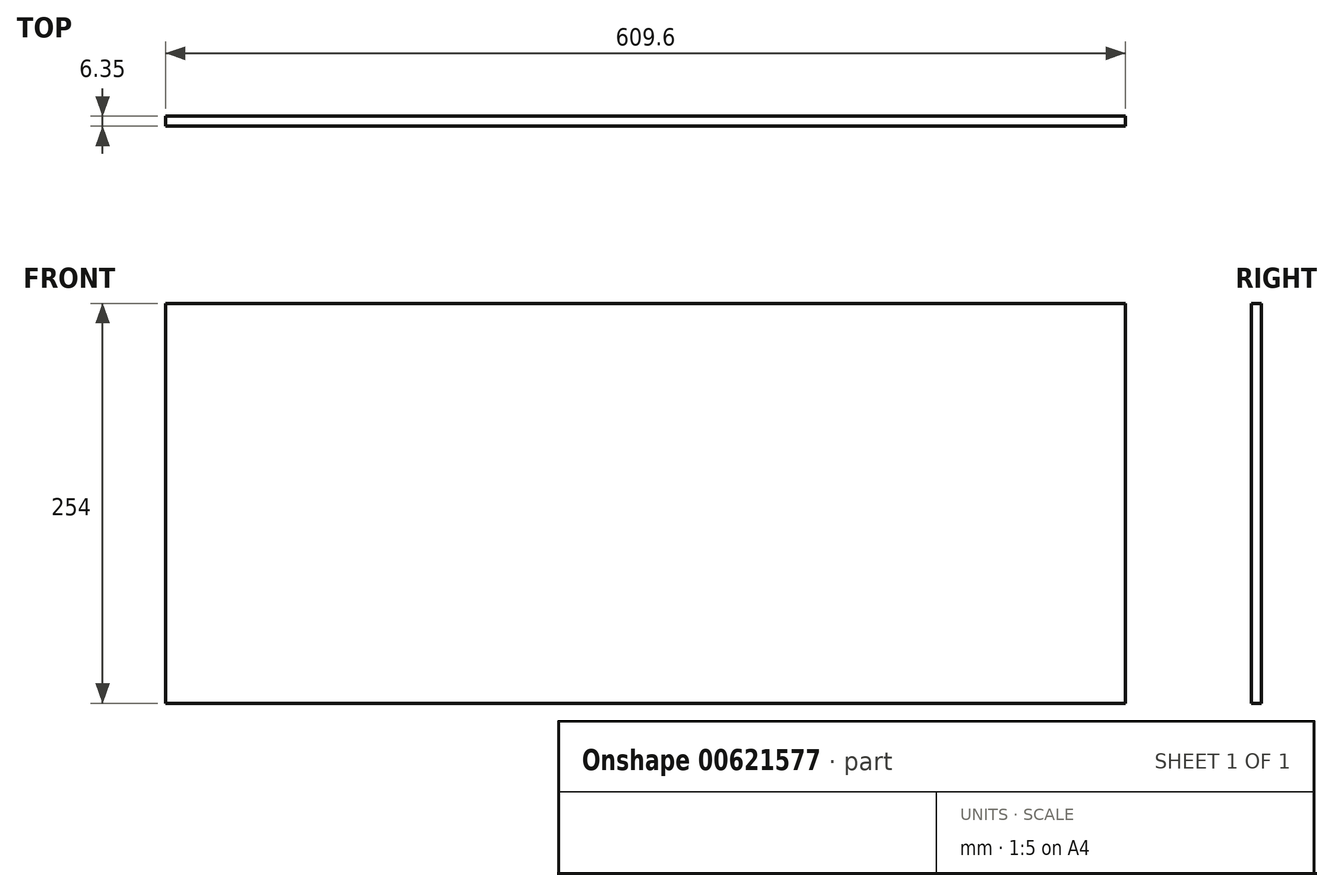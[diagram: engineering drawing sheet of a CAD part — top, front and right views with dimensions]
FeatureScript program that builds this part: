
annotation { "Feature Type Name" : "Feature", "Feature Type Description" : "" }
export const myFeature = defineFeature(function(context is Context, id is Id, definition is map)
    precondition{}
    {
        {
            var Q0;
            Q0=qCreatedBy(makeId("Front.planeOp"),FACE);
            var sketch = newSketch(context, id + "F0", { "sketchPlane" : qUnion([Q0])});
            skLineSegment(sketch, "E0.bottom", {"start": v(308.6, 127) * mm, "end": v(-301, 127) * mm});
            skLineSegment(sketch, "E0.top", {"start": v(308.6, -127) * mm, "end": v(-301, -127) * mm});
            skLineSegment(sketch, "E0.left", {"start": v(308.6, 127) * mm, "end": v(308.6, -127) * mm});
            skLineSegment(sketch, "E0.right", {"start": v(-301, 127) * mm, "end": v(-301, -127) * mm});
            skPoint(sketch, "E0.middle", {"position": v(3.8, 0) * mm});
            skSolve(sketch);
        }
        {
            var Q0;
            Q0 = qSketchRegion(id + "F0", true);
            extrude(context, id + "F1", {"entities" : qUnion([Q0]), "depth" : 6.35 * mm, "offsetDistance" : 25.4 * mm});
        }
    });
